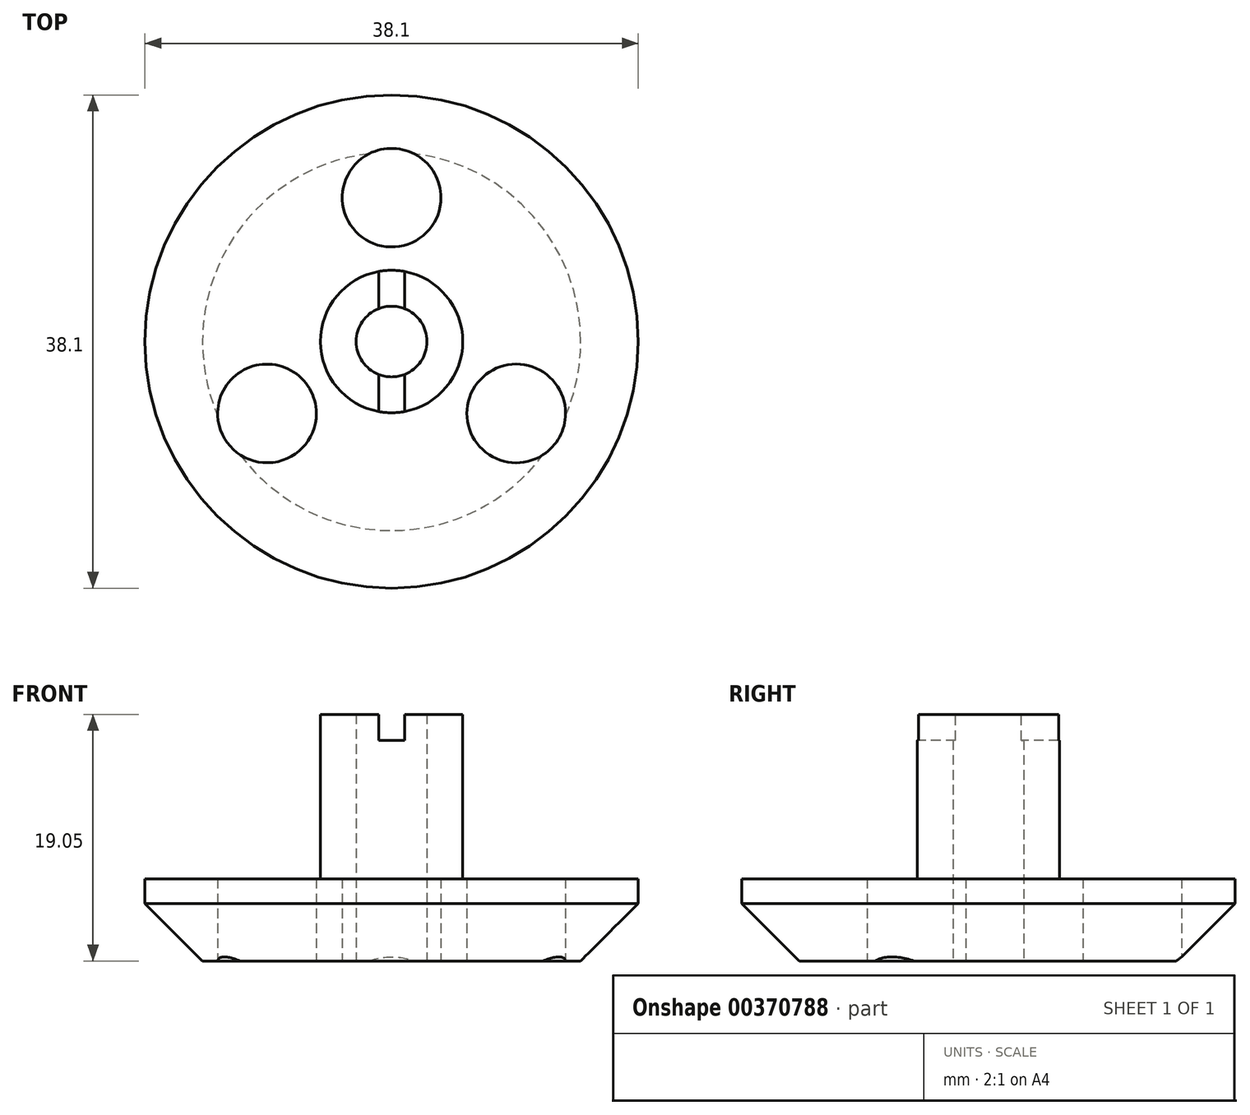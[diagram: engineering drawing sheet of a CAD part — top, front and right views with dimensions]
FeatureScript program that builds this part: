
annotation { "Feature Type Name" : "Feature", "Feature Type Description" : "" }
export const myFeature = defineFeature(function(context is Context, id is Id, definition is map)
    precondition{}
    {
        {
            var Q0;
            Q0=qCreatedBy(makeId("Top.planeOp"),FACE);
            var sketch = newSketch(context, id + "F0", { "sketchPlane" : qUnion([Q0])});
            skCircle(sketch, "E0", {"center": v(0, 0) * mm, "radius": 5.5 * mm});
            skCircle(sketch, "E1", {"center": v(0, 0) * mm, "radius": 2.73 * mm});
            skCircle(sketch, "E2", {"center": v(0, 0) * mm, "radius": 19.05 * mm});
            skCircle(sketch, "E3", {"center": v(0, 0) * mm, "radius": 11.11 * mm, "construction": true});
            skLineSegment(sketch, "E4", {"start": v(0, 0) * mm, "end": v(0, 15.9) * mm, "construction": true});
            skLineSegment(sketch, "E5", {"start": v(0, 0) * mm, "end": v(-17.1, -9.87) * mm, "construction": true});
            skLineSegment(sketch, "E6", {"start": v(0, 0) * mm, "end": v(19.78, -11.42) * mm, "construction": true});
            skCircle(sketch, "E7", {"center": v(0, 11.11) * mm, "radius": 3.81 * mm});
            skCircle(sketch, "E8", {"center": v(9.62, -5.56) * mm, "radius": 3.81 * mm});
            skCircle(sketch, "E9", {"center": v(-9.62, -5.56) * mm, "radius": 3.81 * mm});
            skSolve(sketch);
        }
        {
            var Q0;
            Q0=makeQuery(id+"F0.imprint","IMPRINT",FACE,{"disambiguationData":[TD([[makeQuery(id+"F0.imprint","IMPRINT",EDGE,{"derivedFrom":sQuery(id+"F0.wireOp",EDGE,"E0")}),-1.0]])]});
            extrude(context, id + "F1", {"entities" : qUnion([Q0]), "depth" : 6.35 * mm});
        }
        {
            var Q0;
            Q0=makeQuery(id+"F0.imprint","IMPRINT",FACE,{"disambiguationData":[TD([[makeQuery(id+"F0.imprint","IMPRINT",EDGE,{"derivedFrom":sQuery(id+"F0.wireOp",EDGE,"E0")}),1.0]])]});
            extrude(context, id + "F2", {"entities" : qUnion([Q0]), "operationType" : NewBodyOperationType.ADD, "depth" : 19.05 * mm});
        }
        {
            var Q0;
            Q0=makeQuery(id+"F2.opExtrude","CAP_FACE",FACE,{"disambiguationData":[OSD([sQuery(id+"F0.wireOp",EDGE,"E0"),sQuery(id+"F0.wireOp",EDGE,"E1")])],"isStart":false});
            var sketch = newSketch(context, id + "F3", { "sketchPlane" : qUnion([Q0])});
            skLineSegment(sketch, "E10", {"start": v(1, 5.4) * mm, "end": v(1, -5.4) * mm});
            skLineSegment(sketch, "E11", {"start": v(-1, 5.4) * mm, "end": v(-1, -5.4) * mm});
            skSolve(sketch);
        }
        {
            var Q0;
            {var subQ0=sQuery(id+"F3.wireOp",EDGE,"E10");var subQ1=makeQuery(id+"F2.opExtrude","CAP_EDGE",EDGE,{"disambiguationData":[OSD([sQuery(id+"F0.wireOp",EDGE,"E0")])],"isStart":false});var subQ2=makeQuery(id+"F3.imprint","INTERSECT",VERTEX,{"disambiguationData":[OD(0.0)],"derivedFrom":[subQ1,subQ0]});Q0=makeQuery(id+"F3.imprint","IMPRINT",FACE,{"disambiguationData":[TD([[makeQuery(id+"F3.imprint","IMPRINT",EDGE,{"disambiguationData":[TD([[subQ2,-1.0]])],"derivedFrom":subQ0}),-1.0]])]});}
            var Q1;
            {var subQ0=sQuery(id+"F3.wireOp",EDGE,"E10");var subQ1=makeQuery(id+"F2.opExtrude","CAP_EDGE",EDGE,{"disambiguationData":[OSD([sQuery(id+"F0.wireOp",EDGE,"E0")])],"isStart":false});var subQ2=makeQuery(id+"F3.imprint","INTERSECT",VERTEX,{"disambiguationData":[OD(1.0)],"derivedFrom":[subQ1,subQ0]});Q1=makeQuery(id+"F3.imprint","IMPRINT",FACE,{"disambiguationData":[TD([[makeQuery(id+"F3.imprint","IMPRINT",EDGE,{"disambiguationData":[TD([[subQ2,1.0]])],"derivedFrom":subQ0}),-1.0]])]});}
            extrude(context, id + "F4", {"entities" : qUnion([Q0, Q1]), "operationType" : NewBodyOperationType.REMOVE, "oppositeDirection" : true, "depth" : 2 * mm});
        }
        {
            var Q0;
            Q0=makeQuery(id+"F1.opExtrude","CAP_EDGE",EDGE,{"disambiguationData":[OSD([sQuery(id+"F0.wireOp",EDGE,"E2")])],"isStart":true});
            chamfer(context, id + "F5", {"entities" : qUnion([Q0]), "width" : 4.44 * mm, "tangentPropagation" : true});
        }
    });
